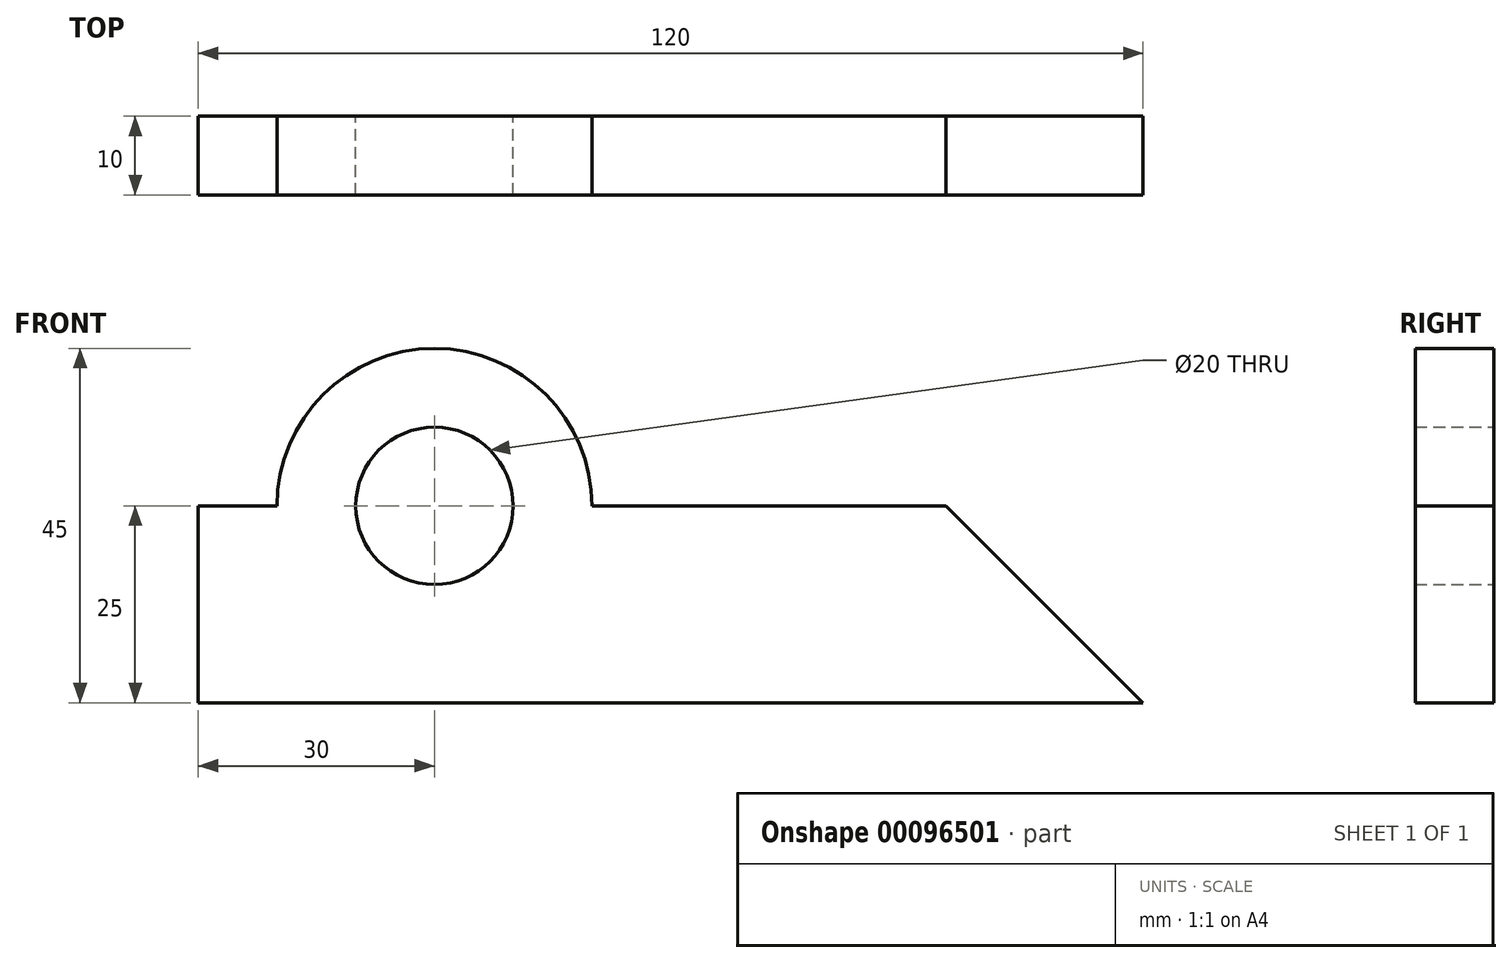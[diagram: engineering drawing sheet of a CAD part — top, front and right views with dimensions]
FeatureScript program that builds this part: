
annotation { "Feature Type Name" : "Feature", "Feature Type Description" : "" }
export const myFeature = defineFeature(function(context is Context, id is Id, definition is map)
    precondition{}
    {
        {
            var Q0;
            Q0=qCreatedBy(makeId("Front.planeOp"),FACE);
            var sketch = newSketch(context, id + "F0", { "sketchPlane" : qUnion([Q0])});
            skLineSegment(sketch, "E0", {"start": v(0, 0) * mm, "end": v(120, 0) * mm});
            skLineSegment(sketch, "E1", {"start": v(120, 0) * mm, "end": v(95, 25) * mm});
            skLineSegment(sketch, "E2", {"start": v(95, 25) * mm, "end": v(50, 25) * mm});
            skLineSegment(sketch, "E3", {"start": v(10, 25) * mm, "end": v(0, 25) * mm});
            skLineSegment(sketch, "E4", {"start": v(0, 25) * mm, "end": v(0, 0) * mm});
            skCircle(sketch, "E5", {"center": v(30, 25) * mm, "radius": 10 * mm});
            skArc(sketch, "E6", {"start": v(50, 25) * mm, "mid": v(30, 45) * mm, "end": v(10, 25) * mm});
            skSolve(sketch);
        }
        {
            var Q0;
            Q0 = qSketchRegion(id + "F0", true);
            extrude(context, id + "F1", {"entities" : qUnion([Q0]), "depth" : 10 * mm});
        }
    });
